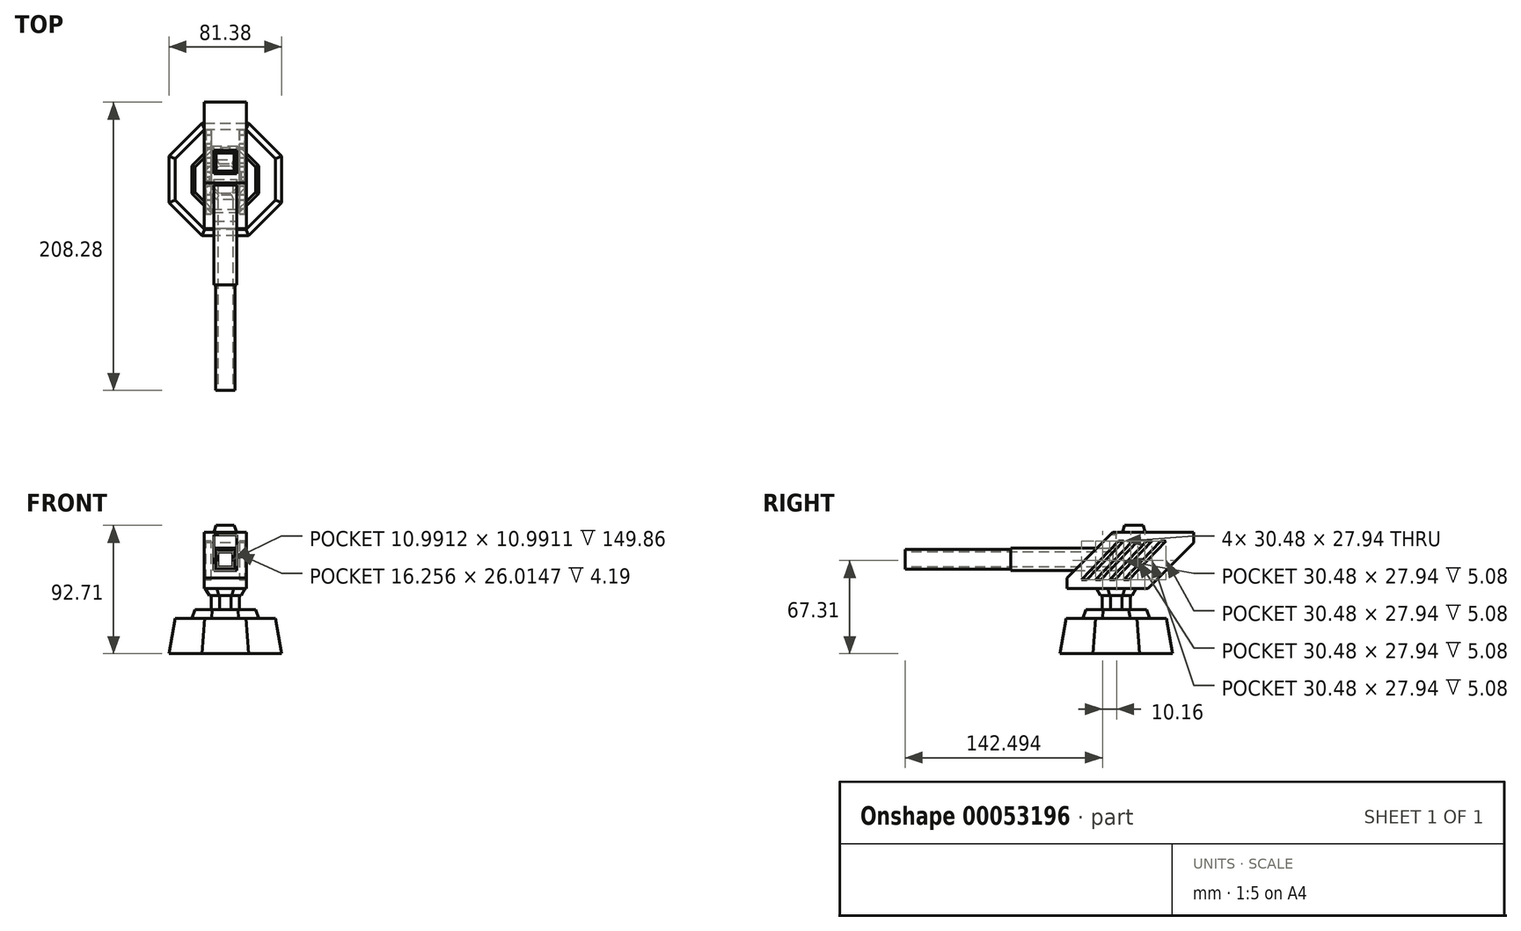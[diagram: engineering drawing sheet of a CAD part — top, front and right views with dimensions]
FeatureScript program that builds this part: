
annotation { "Feature Type Name" : "Feature", "Feature Type Description" : "" }
export const myFeature = defineFeature(function(context is Context, id is Id, definition is map)
    precondition{}
    {
        {
            var Q0;
            Q0=qCreatedBy(makeId("Top.planeOp"),FACE);
            var sketch = newSketch(context, id + "F0", { "sketchPlane" : qUnion([Q0])});
            skLineSegment(sketch, "E0", {"start": v(0, 0) * mm, "end": v(40.69, 16.85) * mm});
            skLineSegment(sketch, "E1", {"start": v(0, 0) * mm, "end": v(0, 37.13) * mm});
            skCircle(sketch, "E2.cCircle", {"center": v(0, 0) * mm, "radius": 44.04 * mm, "construction": true});
            skLineSegment(sketch, "E2.0", {"start": v(40.69, 16.85) * mm, "end": v(40.69, -16.85) * mm});
            skLineSegment(sketch, "E2.1", {"start": v(40.69, -16.85) * mm, "end": v(16.85, -40.69) * mm});
            skLineSegment(sketch, "E2.2", {"start": v(16.85, -40.69) * mm, "end": v(-16.85, -40.69) * mm});
            skLineSegment(sketch, "E2.3", {"start": v(-16.85, -40.69) * mm, "end": v(-40.69, -16.85) * mm});
            skLineSegment(sketch, "E2.4", {"start": v(-40.69, -16.85) * mm, "end": v(-40.69, 16.85) * mm});
            skLineSegment(sketch, "E2.5", {"start": v(-40.69, 16.85) * mm, "end": v(-16.85, 40.69) * mm});
            skLineSegment(sketch, "E2.6", {"start": v(-16.85, 40.69) * mm, "end": v(16.85, 40.69) * mm});
            skLineSegment(sketch, "E2.7", {"start": v(16.85, 40.69) * mm, "end": v(40.69, 16.85) * mm});
            skLineSegment(sketch, "E3", {"start": v(0, 40.69) * mm, "end": v(0, 37.13) * mm});
            skSolve(sketch);
        }
        {
            var Q0;
            Q0 = qSketchRegion(id + "F0", true);
            extrude(context, id + "F1", {"entities" : qUnion([Q0]), "depth" : 25.4 * mm, "hasDraft" : true, "draftAngle" : 10 * degree, "draftPullDirection" : true});
        }
        {
            var Q0;
            Q0=makeQuery(id+"F1.opExtrude","CAP_FACE",FACE,{"disambiguationData":[OSD([sQuery(id+"F0.wireOp",EDGE,"E2.0"),sQuery(id+"F0.wireOp",EDGE,"E2.1"),sQuery(id+"F0.wireOp",EDGE,"E2.2"),sQuery(id+"F0.wireOp",EDGE,"E2.3"),sQuery(id+"F0.wireOp",EDGE,"E2.4"),sQuery(id+"F0.wireOp",EDGE,"E2.5"),sQuery(id+"F0.wireOp",EDGE,"E2.6"),sQuery(id+"F0.wireOp",EDGE,"E2.7")])],"isStart":false});
            var sketch = newSketch(context, id + "F2", { "sketchPlane" : qUnion([Q0])});
            skLineSegment(sketch, "E4", {"start": v(-15, 36.2) * mm, "end": v(-10.01, 24.17) * mm});
            skCircle(sketch, "E5.cCircle", {"center": v(0, 0) * mm, "radius": 26.16 * mm, "construction": true});
            skLineSegment(sketch, "E5.0", {"start": v(-10.01, 24.17) * mm, "end": v(10.01, 24.17) * mm});
            skLineSegment(sketch, "E5.1", {"start": v(10.01, 24.17) * mm, "end": v(24.17, 10.01) * mm});
            skLineSegment(sketch, "E5.2", {"start": v(24.17, 10.01) * mm, "end": v(24.17, -10.01) * mm});
            skLineSegment(sketch, "E5.3", {"start": v(24.17, -10.01) * mm, "end": v(10.01, -24.17) * mm});
            skLineSegment(sketch, "E5.4", {"start": v(10.01, -24.17) * mm, "end": v(-10.01, -24.17) * mm});
            skLineSegment(sketch, "E5.5", {"start": v(-10.01, -24.17) * mm, "end": v(-24.17, -10.01) * mm});
            skLineSegment(sketch, "E5.6", {"start": v(-24.17, -10.01) * mm, "end": v(-24.17, 10.01) * mm});
            skLineSegment(sketch, "E5.7", {"start": v(-24.17, 10.01) * mm, "end": v(-10.01, 24.17) * mm});
            skSolve(sketch);
        }
        {
            var Q0;
            Q0=makeQuery(id+"F2.imprint","IMPRINT",FACE,{"disambiguationData":[TD([[makeQuery(id+"F2.imprint","IMPRINT",EDGE,{"derivedFrom":sQuery(id+"F2.wireOp",EDGE,"E5.0")}),-1.0]])]});
            extrude(context, id + "F3", {"entities" : qUnion([Q0]), "depth" : 6.35 * mm, "hasDraft" : true, "draftAngle" : 20 * degree, "draftPullDirection" : true});
        }
        {
            var Q0;
            Q0=makeQuery(id+"F3.opExtrude","CAP_FACE",FACE,{"disambiguationData":[OSD([sQuery(id+"F2.wireOp",EDGE,"E5.0"),sQuery(id+"F2.wireOp",EDGE,"E5.1"),sQuery(id+"F2.wireOp",EDGE,"E5.2"),sQuery(id+"F2.wireOp",EDGE,"E5.3"),sQuery(id+"F2.wireOp",EDGE,"E5.4"),sQuery(id+"F2.wireOp",EDGE,"E5.5"),sQuery(id+"F2.wireOp",EDGE,"E5.6"),sQuery(id+"F2.wireOp",EDGE,"E5.7")])],"isStart":false});
            var sketch = newSketch(context, id + "F4", { "sketchPlane" : qUnion([Q0])});
            skLineSegment(sketch, "E6", {"start": v(-21.86, 0) * mm, "end": v(-14.37, 0) * mm});
            skPoint(sketch, "E6.endSnap0", {"position": v(-21.86, 0) * mm});
            skLineSegment(sketch, "E7", {"start": v(-9.06, 21.86) * mm, "end": v(-4.16, 10.04) * mm});
            skCircle(sketch, "E8.cCircle", {"center": v(0, 0) * mm, "radius": 10.87 * mm, "construction": true});
            skLineSegment(sketch, "E8.0", {"start": v(-4.16, 10.04) * mm, "end": v(4.16, 10.04) * mm});
            skLineSegment(sketch, "E8.1", {"start": v(4.16, 10.04) * mm, "end": v(10.04, 4.16) * mm});
            skLineSegment(sketch, "E8.2", {"start": v(10.04, 4.16) * mm, "end": v(10.04, -4.16) * mm});
            skLineSegment(sketch, "E8.3", {"start": v(10.04, -4.16) * mm, "end": v(4.16, -10.04) * mm});
            skLineSegment(sketch, "E8.4", {"start": v(4.16, -10.04) * mm, "end": v(-4.16, -10.04) * mm});
            skLineSegment(sketch, "E8.5", {"start": v(-4.16, -10.04) * mm, "end": v(-10.04, -4.16) * mm});
            skLineSegment(sketch, "E8.6", {"start": v(-10.04, -4.16) * mm, "end": v(-10.04, 4.16) * mm});
            skLineSegment(sketch, "E8.7", {"start": v(-10.04, 4.16) * mm, "end": v(-4.16, 10.04) * mm});
            skSolve(sketch);
        }
        {
            var Q0;
            Q0 = qSketchRegion(id + "F4", true);
            extrude(context, id + "F5", {"entities" : qUnion([Q0]), "depth" : 10.16 * mm});
        }
        {
            var Q0;
            Q0=makeQuery(id+"F5.opExtrude","CAP_FACE",FACE,{"disambiguationData":[OSD([sQuery(id+"F4.wireOp",EDGE,"E8.0"),sQuery(id+"F4.wireOp",EDGE,"E8.1"),sQuery(id+"F4.wireOp",EDGE,"E8.2"),sQuery(id+"F4.wireOp",EDGE,"E8.3"),sQuery(id+"F4.wireOp",EDGE,"E8.4"),sQuery(id+"F4.wireOp",EDGE,"E8.5"),sQuery(id+"F4.wireOp",EDGE,"E8.6"),sQuery(id+"F4.wireOp",EDGE,"E8.7")])],"isStart":false});
            var sketch = newSketch(context, id + "F6", { "sketchPlane" : qUnion([Q0])});
            skLineSegment(sketch, "E9", {"start": v(-4.16, 10.04) * mm, "end": v(-4.76, 11.5) * mm});
            skCircle(sketch, "E10.cCircle", {"center": v(0, 0) * mm, "radius": 12.44 * mm, "construction": true});
            skLineSegment(sketch, "E10.0", {"start": v(-4.76, 11.5) * mm, "end": v(4.76, 11.5) * mm});
            skLineSegment(sketch, "E10.1", {"start": v(4.76, 11.5) * mm, "end": v(11.5, 4.76) * mm});
            skLineSegment(sketch, "E10.2", {"start": v(11.5, 4.76) * mm, "end": v(11.5, -4.76) * mm});
            skLineSegment(sketch, "E10.3", {"start": v(11.5, -4.76) * mm, "end": v(4.76, -11.5) * mm});
            skLineSegment(sketch, "E10.4", {"start": v(4.76, -11.5) * mm, "end": v(-4.76, -11.5) * mm});
            skLineSegment(sketch, "E10.5", {"start": v(-4.76, -11.5) * mm, "end": v(-11.5, -4.76) * mm});
            skLineSegment(sketch, "E10.6", {"start": v(-11.5, -4.76) * mm, "end": v(-11.5, 4.76) * mm});
            skLineSegment(sketch, "E10.7", {"start": v(-11.5, 4.76) * mm, "end": v(-4.76, 11.5) * mm});
            skSolve(sketch);
        }
        {
            var Q0;
            Q0 = qSketchRegion(id + "F6", true);
            extrude(context, id + "F7", {"entities" : qUnion([Q0]), "depth" : 5.08 * mm, "hasDraft" : true, "draftAngle" : 30 * degree});
        }
        {
            var Q0;
            Q0=qCreatedBy(makeId("Right.planeOp"),FACE);
            var sketch = newSketch(context, id + "F8", { "sketchPlane" : qUnion([Q0])});
            skLineSegment(sketch, "E11.0", {"start": v(5.97, 47) * mm, "end": v(-5.97, 47) * mm});
            skLineSegment(sketch, "E12", {"start": v(-5.97, 47) * mm, "end": v(-35.56, 47) * mm});
            skLineSegment(sketch, "E13", {"start": v(-35.56, 47) * mm, "end": v(22.86, 47) * mm});
            skPoint(sketch, "E14", {"position": v(0, 47) * mm});
            skLineSegment(sketch, "E15", {"start": v(-35.56, 47) * mm, "end": v(-35.56, 87.63) * mm});
            skLineSegment(sketch, "E16", {"start": v(-2.54, 87.63) * mm, "end": v(56.7, 87.63) * mm});
            skLineSegment(sketch, "E17", {"start": v(55.88, 47) * mm, "end": v(55.88, 87.63) * mm});
            skPoint(sketch, "E18", {"position": v(55.88, 80.01) * mm});
            skLineSegment(sketch, "E19", {"start": v(55.88, 80.01) * mm, "end": v(22.86, 47) * mm});
            skPoint(sketch, "E20", {"position": v(-35.56, 54.61) * mm});
            skLineSegment(sketch, "E21", {"start": v(-35.56, 54.61) * mm, "end": v(-2.54, 87.63) * mm});
            skLineSegment(sketch, "E22", {"start": v(55.88, 87.63) * mm, "end": v(56.7, 87.63) * mm});
            skSolve(sketch);
        }
        {
            var Q0;
            Q0 = qSketchRegion(id + "F8", true);
            extrude(context, id + "F9", {"entities" : qUnion([Q0]), "endBound" : BoundingType.SYMMETRIC, "depth" : 30.48 * mm});
        }
        {
            var Q0;
            Q0=makeQuery(id+"F9.opExtrude","SWEPT_FACE",FACE,{"disambiguationData":[OSD([sQuery(id+"F8.wireOp",EDGE,"E15")])]});
            var sketch = newSketch(context, id + "F10", { "sketchPlane" : qUnion([Q0])});
            skLineSegment(sketch, "E23.0", {"start": v(15.24, 54.61) * mm, "end": v(-15.24, 54.61) * mm});
            skPoint(sketch, "E24", {"position": v(-8.13, 54.61) * mm});
            skPoint(sketch, "E25", {"position": v(8.13, 54.61) * mm});
            skLineSegment(sketch, "E26", {"start": v(-8.13, 54.61) * mm, "end": v(-8.13, 85.98) * mm});
            skLineSegment(sketch, "E27", {"start": v(-8.13, 85.98) * mm, "end": v(10.84, 85.98) * mm});
            skLineSegment(sketch, "E28", {"start": v(8.13, 54.61) * mm, "end": v(8.13, 85.98) * mm});
            skLineSegment(sketch, "E29", {"start": v(-8.13, 59.97) * mm, "end": v(8.13, 59.97) * mm});
            skSolve(sketch);
        }
        {
            var Q0;
            {var subQ3=sQuery(id+"F10.wireOp",EDGE,"E29");Q0=makeQuery(id+"F10.imprint","IMPRINT",FACE,{"disambiguationData":[TD([[makeQuery(id+"F10.imprint","IMPRINT",EDGE,{"derivedFrom":subQ3}),1.0]])]});}
            extrude(context, id + "F11", {"entities" : qUnion([Q0]), "operationType" : NewBodyOperationType.REMOVE, "oppositeDirection" : true, "depth" : 35.56 * mm});
        }
        {
            var Q0;
            Q0=makeQuery(id+"F11.boolean.opBoolean","COPY",FACE,{"derivedFrom":makeQuery(id+"F11.opExtrude","CAP_FACE",FACE,{"disambiguationData":[OSD([sQuery(id+"F10.wireOp",EDGE,"E23.0"),sQuery(id+"F10.wireOp",EDGE,"E26"),sQuery(id+"F10.wireOp",EDGE,"E27"),sQuery(id+"F10.wireOp",EDGE,"E28")])],"isStart":false})});
            var sketch = newSketch(context, id + "F12", { "sketchPlane" : qUnion([Q0])});
            skLineSegment(sketch, "E30.0", {"start": v(-8.13, 76.22) * mm, "end": v(-8.13, 85.98) * mm});
            skLineSegment(sketch, "E31.0", {"start": v(8.13, 76.22) * mm, "end": v(8.13, 85.98) * mm});
            skLineSegment(sketch, "E32", {"start": v(-8.13, 76.22) * mm, "end": v(8.13, 76.22) * mm});
            skLineSegment(sketch, "E33.0", {"start": v(-8.13, 59.97) * mm, "end": v(-8.13, 85.98) * mm});
            skLineSegment(sketch, "E34.0", {"start": v(8.13, 59.97) * mm, "end": v(8.13, 85.98) * mm});
            skLineSegment(sketch, "E35", {"start": v(-8.13, 59.97) * mm, "end": v(8.13, 59.97) * mm});
            skSolve(sketch);
        }
        {
            var Q0;
            Q0 = qSketchRegion(id + "F12", true);
            extrude(context, id + "F13", {"entities" : qUnion([Q0]), "depth" : 76.2 * mm});
        }
        {
            var Q0;
            Q0=makeQuery(id+"F13.opExtrude","CAP_FACE",FACE,{"disambiguationData":[OSD([sQuery(id+"F12.wireOp",EDGE,"E32"),sQuery(id+"F12.wireOp",EDGE,"E33.0"),sQuery(id+"F12.wireOp",EDGE,"E34.0"),sQuery(id+"F12.wireOp",EDGE,"E35")])],"isStart":false});
            var sketch = newSketch(context, id + "F14", { "sketchPlane" : qUnion([Q0])});
            skLineSegment(sketch, "E36.rect.bottom", {"start": v(-7.11, 75.2) * mm, "end": v(7.11, 75.2) * mm});
            skLineSegment(sketch, "E36.rect.top", {"start": v(-7.11, 60.98) * mm, "end": v(7.11, 60.98) * mm});
            skLineSegment(sketch, "E36.rect.left", {"start": v(-7.11, 75.2) * mm, "end": v(-7.11, 60.98) * mm});
            skLineSegment(sketch, "E36.rect.right", {"start": v(7.11, 75.2) * mm, "end": v(7.11, 60.98) * mm});
            skPoint(sketch, "E36.rect.middle", {"position": v(0, 68.1) * mm});
            skPoint(sketch, "E36.rect.middle.positionSnap0", {"position": v(-8.13, 68.1) * mm});
            skPoint(sketch, "E36.rect.middle.positionSnap1", {"position": v(0, 76.22) * mm});
            skPoint(sketch, "E36.rect.centerSnap0", {"position": v(-8.13, 68.1) * mm});
            skPoint(sketch, "E36.rect.centerSnap1", {"position": v(0, 76.22) * mm});
            skSolve(sketch);
        }
        {
            var Q0;
            Q0 = qSketchRegion(id + "F14", true);
            extrude(context, id + "F15", {"entities" : qUnion([Q0]), "operationType" : NewBodyOperationType.ADD, "depth" : 76.2 * mm, "hasDraft" : true, "draftAngle" : 0 * degree, "draftPullDirection" : true});
        }
        {
            var Q0;
            Q0=makeQuery(id+"F15.opExtrude","CAP_FACE",FACE,{"disambiguationData":[OSD([sQuery(id+"F14.wireOp",EDGE,"E36.rect.bottom"),sQuery(id+"F14.wireOp",EDGE,"E36.rect.top"),sQuery(id+"F14.wireOp",EDGE,"E36.rect.left"),sQuery(id+"F14.wireOp",EDGE,"E36.rect.right")])],"isStart":false});
            var sketch = newSketch(context, id + "F16", { "sketchPlane" : qUnion([Q0])});
            skLineSegment(sketch, "E37", {"start": v(-7.11, 75.2) * mm, "end": v(-5.5, 73.59) * mm});
            skLineSegment(sketch, "E38.rect.bottom", {"start": v(-5.5, 73.59) * mm, "end": v(5.5, 73.59) * mm});
            skLineSegment(sketch, "E38.rect.top", {"start": v(-5.5, 62.6) * mm, "end": v(5.5, 62.6) * mm});
            skLineSegment(sketch, "E38.rect.left", {"start": v(-5.5, 73.59) * mm, "end": v(-5.5, 62.6) * mm});
            skLineSegment(sketch, "E38.rect.right", {"start": v(5.5, 73.59) * mm, "end": v(5.5, 62.6) * mm});
            skPoint(sketch, "E38.rect.middle", {"position": v(0, 68.1) * mm});
            skPoint(sketch, "E38.rect.middle.positionSnap0", {"position": v(-7.11, 68.1) * mm});
            skPoint(sketch, "E38.rect.middle.positionSnap1", {"position": v(0, 75.2) * mm});
            skPoint(sketch, "E38.rect.centerSnap0", {"position": v(-7.11, 68.1) * mm});
            skPoint(sketch, "E38.rect.centerSnap1", {"position": v(0, 75.2) * mm});
            skSolve(sketch);
        }
        {
            var Q0;
            Q0 = qSketchRegion(id + "F16", true);
            extrude(context, id + "F17", {"entities" : qUnion([Q0]), "operationType" : NewBodyOperationType.REMOVE, "oppositeDirection" : true, "depth" : 149.86 * mm});
        }
        {
            var Q0;
            Q0=makeQuery(id+"F9.opExtrude","SWEPT_FACE",FACE,{"disambiguationData":[OSD([sQuery(id+"F8.wireOp",EDGE,"E16")])]});
            var sketch = newSketch(context, id + "F18", { "sketchPlane" : qUnion([Q0])});
            skLineSegment(sketch, "E39.rect.bottom", {"start": v(-8.38, 21.08) * mm, "end": v(8.38, 21.08) * mm});
            skLineSegment(sketch, "E39.rect.top", {"start": v(-8.38, 4.32) * mm, "end": v(8.38, 4.32) * mm});
            skLineSegment(sketch, "E39.rect.left", {"start": v(-8.38, 21.08) * mm, "end": v(-8.38, 4.32) * mm});
            skLineSegment(sketch, "E39.rect.right", {"start": v(8.38, 21.08) * mm, "end": v(8.38, 4.32) * mm});
            skPoint(sketch, "E39.rect.middle", {"position": v(0, 12.7) * mm});
            skSolve(sketch);
        }
        {
            var Q0;
            Q0 = qSketchRegion(id + "F18", true);
            extrude(context, id + "F19", {"entities" : qUnion([Q0]), "depth" : 5.08 * mm, "hasDraft" : true, "draftAngle" : 20 * degree, "draftPullDirection" : true});
        }
        {
            var Q0;
            Q0=makeQuery(id+"F9.opExtrude","CAP_FACE",FACE,{"disambiguationData":[OSD([sQuery(id+"F8.wireOp",EDGE,"E13"),sQuery(id+"F8.wireOp",EDGE,"E15"),sQuery(id+"F8.wireOp",EDGE,"E16"),sQuery(id+"F8.wireOp",EDGE,"E17"),sQuery(id+"F8.wireOp",EDGE,"E19"),sQuery(id+"F8.wireOp",EDGE,"E21")])],"isStart":false});
            var sketch = newSketch(context, id + "F20", { "sketchPlane" : qUnion([Q0])});
            skPoint(sketch, "E40", {"position": v(-35.56, 53.34) * mm});
            skPoint(sketch, "E41", {"position": v(-8.89, 81.28) * mm});
            skPoint(sketch, "E42", {"position": v(1.52, 81.28) * mm});
            skPoint(sketch, "E43", {"position": v(5.33, 81.28) * mm});
            skPoint(sketch, "E44", {"position": v(11.68, 81.28) * mm});
            skPoint(sketch, "E45", {"position": v(15.5, 81.28) * mm});
            skPoint(sketch, "E46", {"position": v(21.84, 81.28) * mm});
            skPoint(sketch, "E47", {"position": v(25.65, 81.28) * mm});
            skPoint(sketch, "E48", {"position": v(-21.34, 53.34) * mm});
            skPoint(sketch, "E49", {"position": v(-25.15, 53.34) * mm});
            skPoint(sketch, "E50", {"position": v(-14.99, 53.34) * mm});
            skPoint(sketch, "E51", {"position": v(-11.18, 53.34) * mm});
            skPoint(sketch, "E52", {"position": v(-4.83, 53.34) * mm});
            skPoint(sketch, "E53", {"position": v(-1.02, 53.34) * mm});
            skLineSegment(sketch, "E54", {"start": v(1.52, 81.28) * mm, "end": v(-25.15, 53.34) * mm});
            skLineSegment(sketch, "E55", {"start": v(-21.34, 53.34) * mm, "end": v(-25.15, 53.34) * mm});
            skLineSegment(sketch, "E56", {"start": v(-21.34, 53.34) * mm, "end": v(5.33, 81.28) * mm});
            skLineSegment(sketch, "E57", {"start": v(5.33, 81.28) * mm, "end": v(1.52, 81.28) * mm});
            skLineSegment(sketch, "E58", {"start": v(11.68, 81.28) * mm, "end": v(-14.99, 53.34) * mm});
            skLineSegment(sketch, "E59", {"start": v(-11.18, 53.34) * mm, "end": v(-14.99, 53.34) * mm});
            skLineSegment(sketch, "E60", {"start": v(15.5, 81.28) * mm, "end": v(-11.18, 53.34) * mm});
            skLineSegment(sketch, "E61", {"start": v(11.68, 81.28) * mm, "end": v(15.5, 81.28) * mm});
            skLineSegment(sketch, "E62", {"start": v(21.84, 81.28) * mm, "end": v(-4.83, 53.34) * mm});
            skLineSegment(sketch, "E63", {"start": v(-1.02, 53.34) * mm, "end": v(25.65, 81.28) * mm});
            skPoint(sketch, "E64", {"position": v(32, 81.28) * mm});
            skPoint(sketch, "E65", {"position": v(35.81, 81.28) * mm});
            skPoint(sketch, "E66", {"position": v(5.33, 53.34) * mm});
            skPoint(sketch, "E67", {"position": v(9.14, 53.34) * mm});
            skLineSegment(sketch, "E68", {"start": v(5.33, 53.34) * mm, "end": v(32, 81.28) * mm});
            skLineSegment(sketch, "E69", {"start": v(32, 81.28) * mm, "end": v(35.81, 81.28) * mm});
            skLineSegment(sketch, "E70", {"start": v(35.81, 81.28) * mm, "end": v(9.14, 53.34) * mm});
            skLineSegment(sketch, "E71", {"start": v(9.14, 53.34) * mm, "end": v(5.33, 53.34) * mm});
            skLineSegment(sketch, "E72", {"start": v(-1.02, 53.34) * mm, "end": v(-4.83, 53.34) * mm});
            skLineSegment(sketch, "E73", {"start": v(21.84, 81.28) * mm, "end": v(25.65, 81.28) * mm});
            skSolve(sketch);
        }
        {
            var Q0;
            Q0 = qSketchRegion(id + "F20", true);
            extrude(context, id + "F21", {"entities" : qUnion([Q0]), "operationType" : NewBodyOperationType.REMOVE, "oppositeDirection" : true, "depth" : 5.08 * mm});
        }
        {
            var Q0;
            Q0=makeQuery(id+"F9.opExtrude","CAP_FACE",FACE,{"disambiguationData":[OSD([sQuery(id+"F8.wireOp",EDGE,"E13"),sQuery(id+"F8.wireOp",EDGE,"E15"),sQuery(id+"F8.wireOp",EDGE,"E16"),sQuery(id+"F8.wireOp",EDGE,"E17"),sQuery(id+"F8.wireOp",EDGE,"E19"),sQuery(id+"F8.wireOp",EDGE,"E21")])],"isStart":true});
            var sketch = newSketch(context, id + "F22", { "sketchPlane" : qUnion([Q0])});
            skLineSegment(sketch, "E74.0.0", {"start": v(-5.33, 81.28) * mm, "end": v(-1.52, 81.28) * mm});
            skLineSegment(sketch, "E74.0.1", {"start": v(-1.52, 81.28) * mm, "end": v(25.15, 53.34) * mm});
            skLineSegment(sketch, "E74.0.2", {"start": v(25.15, 53.34) * mm, "end": v(21.34, 53.34) * mm});
            skLineSegment(sketch, "E74.0.3", {"start": v(21.34, 53.34) * mm, "end": v(-5.33, 81.28) * mm});
            skLineSegment(sketch, "E75.0.0", {"start": v(-15.5, 81.28) * mm, "end": v(-11.68, 81.28) * mm});
            skLineSegment(sketch, "E75.0.1", {"start": v(-11.68, 81.28) * mm, "end": v(14.99, 53.34) * mm});
            skLineSegment(sketch, "E75.0.2", {"start": v(14.99, 53.34) * mm, "end": v(11.18, 53.34) * mm});
            skLineSegment(sketch, "E75.0.3", {"start": v(11.18, 53.34) * mm, "end": v(-15.5, 81.28) * mm});
            skLineSegment(sketch, "E76.0.0", {"start": v(-25.65, 81.28) * mm, "end": v(-21.84, 81.28) * mm});
            skLineSegment(sketch, "E76.0.1", {"start": v(-21.84, 81.28) * mm, "end": v(4.83, 53.34) * mm});
            skLineSegment(sketch, "E76.0.2", {"start": v(4.83, 53.34) * mm, "end": v(1.02, 53.34) * mm});
            skLineSegment(sketch, "E76.0.3", {"start": v(1.02, 53.34) * mm, "end": v(-25.65, 81.28) * mm});
            skLineSegment(sketch, "E77.0.0", {"start": v(-32, 81.28) * mm, "end": v(-5.33, 53.34) * mm});
            skLineSegment(sketch, "E77.0.1", {"start": v(-5.33, 53.34) * mm, "end": v(-9.14, 53.34) * mm});
            skLineSegment(sketch, "E77.0.2", {"start": v(-9.14, 53.34) * mm, "end": v(-35.81, 81.28) * mm});
            skLineSegment(sketch, "E77.0.3", {"start": v(-35.81, 81.28) * mm, "end": v(-32, 81.28) * mm});
            skSolve(sketch);
        }
        {
            var Q0;
            Q0 = qSketchRegion(id + "F22", true);
            extrude(context, id + "F23", {"entities" : qUnion([Q0]), "operationType" : NewBodyOperationType.REMOVE, "oppositeDirection" : true, "depth" : 5.08 * mm});
        }
        {
            var Q0;
            Q0=makeQuery(id+"F23.boolean.opBoolean","COPY",FACE,{"derivedFrom":makeQuery(id+"F23.opExtrude","CAP_FACE",FACE,{"disambiguationData":[OSD([sQuery(id+"F22.wireOp",EDGE,"E74.0.0"),sQuery(id+"F22.wireOp",EDGE,"E74.0.1"),sQuery(id+"F22.wireOp",EDGE,"E74.0.2"),sQuery(id+"F22.wireOp",EDGE,"E74.0.3")])],"isStart":false})});
            var sketch = newSketch(context, id + "F24", { "sketchPlane" : qUnion([Q0])});
            skLineSegment(sketch, "E78.0.0", {"start": v(-11.68, 81.28) * mm, "end": v(-15.5, 81.28) * mm});
            skLineSegment(sketch, "E78.0.1", {"start": v(-15.5, 81.28) * mm, "end": v(11.18, 53.34) * mm});
            skLineSegment(sketch, "E78.0.2", {"start": v(11.18, 53.34) * mm, "end": v(14.99, 53.34) * mm});
            skLineSegment(sketch, "E78.0.3", {"start": v(14.99, 53.34) * mm, "end": v(-11.68, 81.28) * mm});
            skLineSegment(sketch, "E79.0.0", {"start": v(-1.52, 81.28) * mm, "end": v(-5.33, 81.28) * mm});
            skLineSegment(sketch, "E79.0.1", {"start": v(-5.33, 81.28) * mm, "end": v(21.34, 53.34) * mm});
            skLineSegment(sketch, "E79.0.2", {"start": v(21.34, 53.34) * mm, "end": v(25.15, 53.34) * mm});
            skLineSegment(sketch, "E79.0.3", {"start": v(25.15, 53.34) * mm, "end": v(-1.52, 81.28) * mm});
            skLineSegment(sketch, "E80.0.0", {"start": v(-21.84, 81.28) * mm, "end": v(-25.65, 81.28) * mm});
            skLineSegment(sketch, "E80.0.1", {"start": v(-25.65, 81.28) * mm, "end": v(1.02, 53.34) * mm});
            skLineSegment(sketch, "E80.0.2", {"start": v(1.02, 53.34) * mm, "end": v(4.83, 53.34) * mm});
            skLineSegment(sketch, "E80.0.3", {"start": v(4.83, 53.34) * mm, "end": v(-21.84, 81.28) * mm});
            skLineSegment(sketch, "E81.0.0", {"start": v(-5.33, 53.34) * mm, "end": v(-32, 81.28) * mm});
            skLineSegment(sketch, "E81.0.1", {"start": v(-32, 81.28) * mm, "end": v(-35.81, 81.28) * mm});
            skLineSegment(sketch, "E81.0.2", {"start": v(-35.81, 81.28) * mm, "end": v(-9.14, 53.34) * mm});
            skLineSegment(sketch, "E81.0.3", {"start": v(-9.14, 53.34) * mm, "end": v(-5.33, 53.34) * mm});
            skSolve(sketch);
        }
        {
            var Q0;
            Q0 = qSketchRegion(id + "F24", true);
            extrude(context, id + "F25", {"entities" : qUnion([Q0]), "depth" : 3.8 * mm});
        }
        {
            var Q0;
            Q0=makeQuery(id+"F21.boolean.opBoolean","COPY",FACE,{"derivedFrom":makeQuery(id+"F21.opExtrude","CAP_FACE",FACE,{"disambiguationData":[OSD([sQuery(id+"F20.wireOp",EDGE,"E58"),sQuery(id+"F20.wireOp",EDGE,"E59"),sQuery(id+"F20.wireOp",EDGE,"E60"),sQuery(id+"F20.wireOp",EDGE,"E61")])],"isStart":false})});
            var sketch = newSketch(context, id + "F26", { "sketchPlane" : qUnion([Q0])});
            skLineSegment(sketch, "E82.0.0", {"start": v(5.33, 81.28) * mm, "end": v(1.52, 81.28) * mm});
            skLineSegment(sketch, "E82.0.1", {"start": v(1.52, 81.28) * mm, "end": v(-25.15, 53.34) * mm});
            skLineSegment(sketch, "E82.0.2", {"start": v(-25.15, 53.34) * mm, "end": v(-21.34, 53.34) * mm});
            skLineSegment(sketch, "E82.0.3", {"start": v(-21.34, 53.34) * mm, "end": v(5.33, 81.28) * mm});
            skLineSegment(sketch, "E83.0.0", {"start": v(15.5, 81.28) * mm, "end": v(11.68, 81.28) * mm});
            skLineSegment(sketch, "E83.0.1", {"start": v(11.68, 81.28) * mm, "end": v(-14.99, 53.34) * mm});
            skLineSegment(sketch, "E83.0.2", {"start": v(-14.99, 53.34) * mm, "end": v(-11.18, 53.34) * mm});
            skLineSegment(sketch, "E83.0.3", {"start": v(-11.18, 53.34) * mm, "end": v(15.5, 81.28) * mm});
            skLineSegment(sketch, "E84.0.0", {"start": v(25.65, 81.28) * mm, "end": v(21.84, 81.28) * mm});
            skLineSegment(sketch, "E84.0.1", {"start": v(21.84, 81.28) * mm, "end": v(-4.83, 53.34) * mm});
            skLineSegment(sketch, "E84.0.2", {"start": v(-4.83, 53.34) * mm, "end": v(-1.02, 53.34) * mm});
            skLineSegment(sketch, "E84.0.3", {"start": v(-1.02, 53.34) * mm, "end": v(25.65, 81.28) * mm});
            skLineSegment(sketch, "E85.0.0", {"start": v(32, 81.28) * mm, "end": v(5.33, 53.34) * mm});
            skLineSegment(sketch, "E85.0.1", {"start": v(5.33, 53.34) * mm, "end": v(9.14, 53.34) * mm});
            skLineSegment(sketch, "E85.0.2", {"start": v(9.14, 53.34) * mm, "end": v(35.81, 81.28) * mm});
            skLineSegment(sketch, "E85.0.3", {"start": v(35.81, 81.28) * mm, "end": v(32, 81.28) * mm});
            skSolve(sketch);
        }
        {
            var Q0;
            Q0 = qSketchRegion(id + "F26", true);
            extrude(context, id + "F27", {"entities" : qUnion([Q0]), "depth" : 3.8 * mm});
        }
    });
